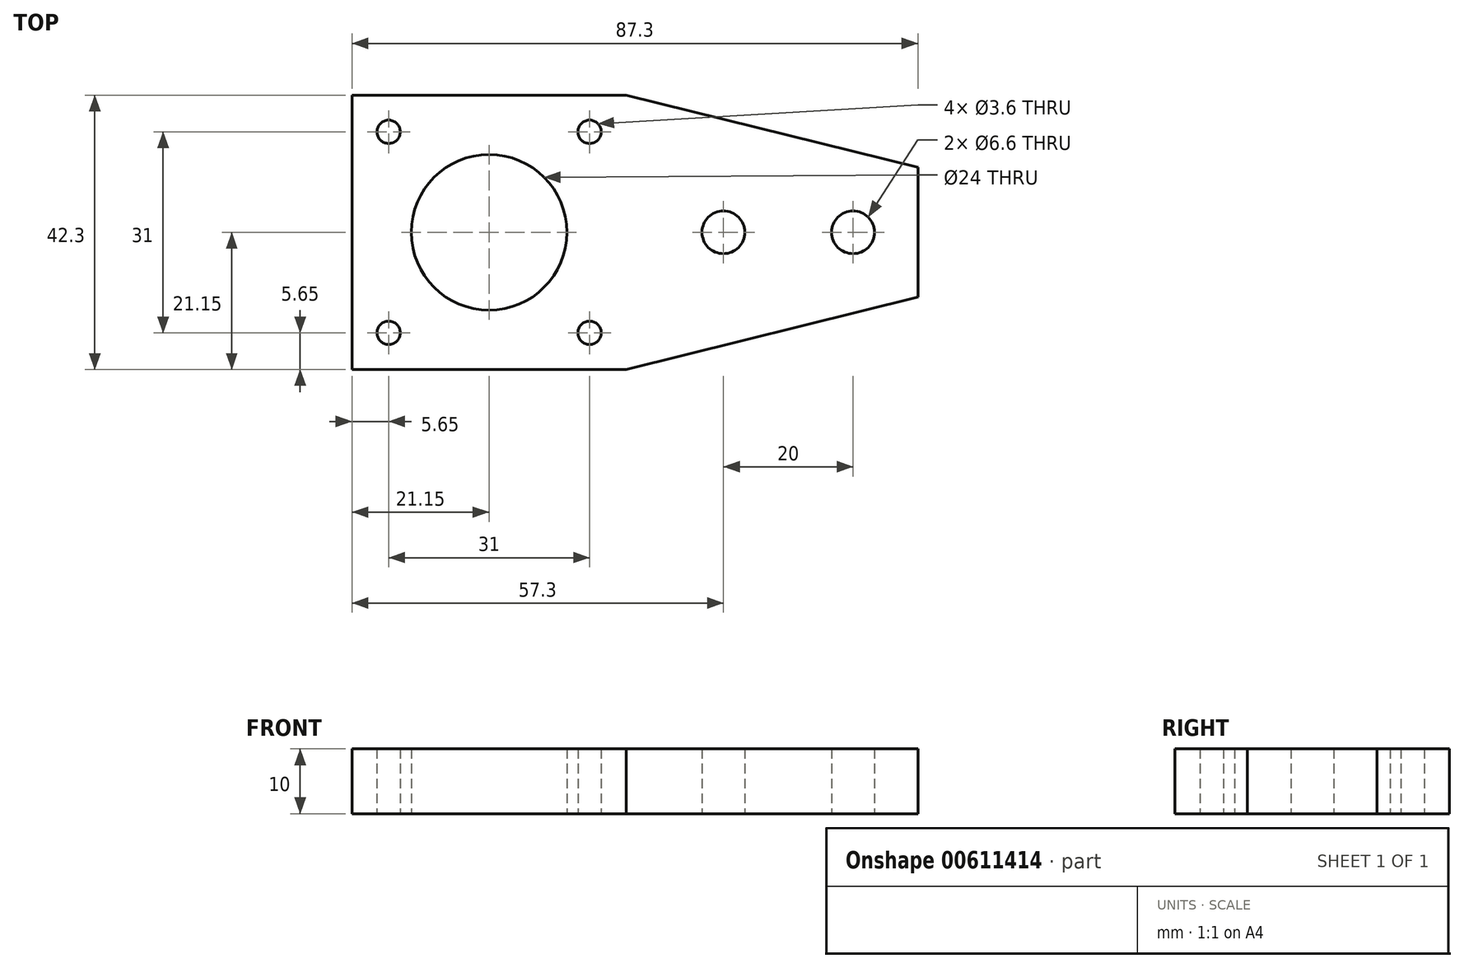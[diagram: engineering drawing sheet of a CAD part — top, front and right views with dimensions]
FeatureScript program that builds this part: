
annotation { "Feature Type Name" : "Feature", "Feature Type Description" : "" }
export const myFeature = defineFeature(function(context is Context, id is Id, definition is map)
    precondition{}
    {
        {
            var Q0;
            Q0=qCreatedBy(makeId("Top.planeOp"),FACE);
            var sketch = newSketch(context, id + "F0", { "sketchPlane" : qUnion([Q0])});
            skLineSegment(sketch, "E0.bottom", {"start": v(21.15, 21.15) * mm, "end": v(-21.15, 21.15) * mm});
            skLineSegment(sketch, "E0.top", {"start": v(21.15, -21.15) * mm, "end": v(-21.15, -21.15) * mm});
            skLineSegment(sketch, "E0.left", {"start": v(21.15, 21.15) * mm, "end": v(21.15, -21.15) * mm});
            skLineSegment(sketch, "E0.right", {"start": v(-21.15, 21.15) * mm, "end": v(-21.15, -21.15) * mm});
            skPoint(sketch, "E0.middle", {"position": v(0, 0) * mm});
            skLineSegment(sketch, "E1.bottom", {"start": v(15.5, 15.5) * mm, "end": v(-15.5, 15.5) * mm});
            skLineSegment(sketch, "E1.top", {"start": v(15.5, -15.5) * mm, "end": v(-15.5, -15.5) * mm});
            skLineSegment(sketch, "E1.left", {"start": v(15.5, 15.5) * mm, "end": v(15.5, -15.5) * mm});
            skLineSegment(sketch, "E1.right", {"start": v(-15.5, 15.5) * mm, "end": v(-15.5, -15.5) * mm});
            skCircle(sketch, "E2", {"center": v(-15.5, 15.5) * mm, "radius": 1.8 * mm});
            skCircle(sketch, "E3", {"center": v(0, 0) * mm, "radius": 12 * mm});
            skCircle(sketch, "E4.MirrorC", {"center": v(15.5, 15.5) * mm, "radius": 1.8 * mm});
            skCircle(sketch, "E5.MirrorC", {"center": v(15.5, -15.5) * mm, "radius": 1.8 * mm});
            skCircle(sketch, "E6.MirrorC", {"center": v(-15.5, -15.5) * mm, "radius": 1.8 * mm});
            skLineSegment(sketch, "E7", {"start": v(21.15, 10) * mm, "end": v(66.15, 10) * mm});
            skLineSegment(sketch, "E8", {"start": v(66.15, 10) * mm, "end": v(66.15, -10) * mm});
            skLineSegment(sketch, "E9", {"start": v(66.15, -10) * mm, "end": v(21.15, -10) * mm});
            skCircle(sketch, "E10", {"center": v(36.15, 0) * mm, "radius": 3.3 * mm});
            skCircle(sketch, "E11", {"center": v(56.15, 0) * mm, "radius": 3.3 * mm});
            skLineSegment(sketch, "E12", {"start": v(21.15, 21.15) * mm, "end": v(66.15, 10) * mm});
            skLineSegment(sketch, "E13", {"start": v(21.15, -21.15) * mm, "end": v(66.15, -10) * mm});
            skSolve(sketch);
        }
        {
            var Q0;
            {var subQ1=sQuery(id+"F0.wireOp",EDGE,"E7");Q0=makeQuery(id+"F0.imprint","IMPRINT",FACE,{"disambiguationData":[TD([[makeQuery(id+"F0.imprint","IMPRINT",EDGE,{"derivedFrom":subQ1}),-1.0]])]});}
            var Q1;
            {var subQ2=sQuery(id+"F0.wireOp",EDGE,"E7");Q1=makeQuery(id+"F0.imprint","IMPRINT",FACE,{"disambiguationData":[TD([[makeQuery(id+"F0.imprint","IMPRINT",EDGE,{"derivedFrom":subQ2}),1.0]])]});}
            var Q2;
            {var subQ2=sQuery(id+"F0.wireOp",EDGE,"E9");Q2=makeQuery(id+"F0.imprint","IMPRINT",FACE,{"disambiguationData":[TD([[makeQuery(id+"F0.imprint","IMPRINT",EDGE,{"derivedFrom":subQ2}),1.0]])]});}
            var Q3;
            {var subQ16=sQuery(id+"F0.wireOp",EDGE,"E0.bottom");Q3=makeQuery(id+"F0.imprint","IMPRINT",FACE,{"disambiguationData":[TD([[makeQuery(id+"F0.imprint","IMPRINT",EDGE,{"derivedFrom":subQ16}),1.0]])]});}
            var Q4;
            Q4=makeQuery(id+"F0.imprint","IMPRINT",FACE,{"disambiguationData":[TD([[makeQuery(id+"F0.imprint","IMPRINT",EDGE,{"derivedFrom":sQuery(id+"F0.wireOp",EDGE,"E3")}),-1.0]])]});
            extrude(context, id + "F1", {"entities" : qUnion([Q0, Q1, Q2, Q3, Q4]), "depth" : 10 * mm, "offsetDistance" : 25 * mm});
        }
    });
